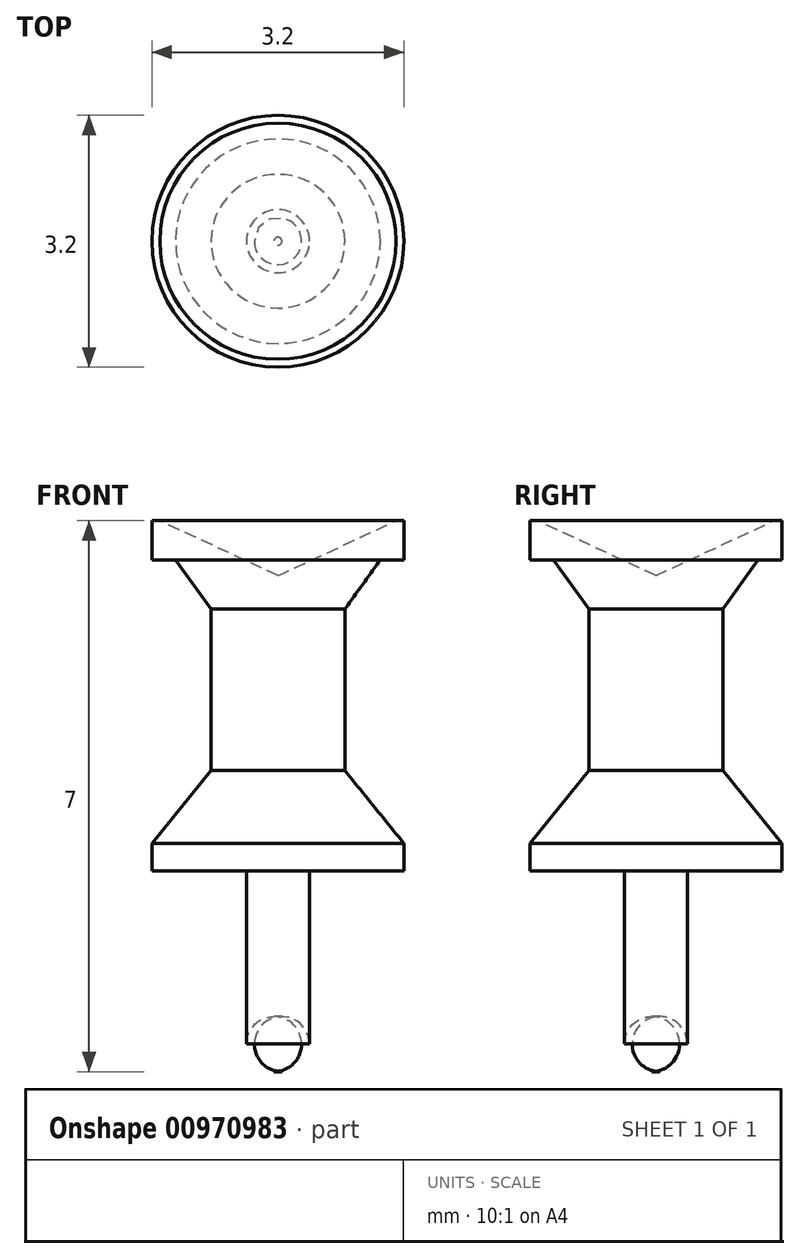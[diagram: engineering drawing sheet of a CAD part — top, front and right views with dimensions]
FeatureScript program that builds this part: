
annotation { "Feature Type Name" : "Feature", "Feature Type Description" : "" }
export const myFeature = defineFeature(function(context is Context, id is Id, definition is map)
    precondition{}
    {
        {
            var Q0;
            Q0=qCreatedBy(makeId("Front.planeOp"),FACE);
            var sketch = newSketch(context, id + "F0", { "sketchPlane" : qUnion([Q0])});
            skLineSegment(sketch, "E0", {"start": v(1.6, 4.45) * mm, "end": v(1.6, 3.95) * mm});
            skLineSegment(sketch, "E1", {"start": v(1.6, 4.45) * mm, "end": v(1.5, 4.45) * mm});
            skLineSegment(sketch, "E2", {"start": v(1.5, 4.45) * mm, "end": v(0, 3.75) * mm});
            skLineSegment(sketch, "E3", {"start": v(1.6, 4.45) * mm, "end": v(1.6, 3.95) * mm, "construction": true});
            skLineSegment(sketch, "E4", {"start": v(1.6, 3.95) * mm, "end": v(1.3, 3.95) * mm});
            skLineSegment(sketch, "E5", {"start": v(1.3, 3.95) * mm, "end": v(0.85, 3.33) * mm});
            skLineSegment(sketch, "E6", {"start": v(1.6, 0.35) * mm, "end": v(0.85, 1.27) * mm});
            skLineSegment(sketch, "E7", {"start": v(0.85, 4.45) * mm, "end": v(0.85, 1.27) * mm, "construction": true});
            skLineSegment(sketch, "E8", {"start": v(0.85, 3.33) * mm, "end": v(0.85, 1.27) * mm});
            skLineSegment(sketch, "E9.trimOffspring", {"start": v(1.6, 0.35) * mm, "end": v(1.6, 0) * mm, "construction": true});
            skLineSegment(sketch, "E10", {"start": v(1.6, 0.35) * mm, "end": v(1.6, 0) * mm});
            skLineSegment(sketch, "E11", {"start": v(0.4, 0) * mm, "end": v(1.6, 0) * mm});
            skPoint(sketch, "E12.start.orphan", {"position": v(0, 0) * mm});
            skLineSegment(sketch, "E13", {"start": v(0.4, 0) * mm, "end": v(0.4, -2.05) * mm});
            skLineSegment(sketch, "E14", {"start": v(0, -2.4) * mm, "end": v(0, 3.75) * mm});
            skLineSegment(sketch, "E15", {"start": v(1.6, 4.45) * mm, "end": v(0, 4.45) * mm, "construction": true});
            skLineSegment(sketch, "E16", {"start": v(0, 4.45) * mm, "end": v(0, -2.55) * mm, "construction": true});
            skLineSegment(sketch, "E17", {"start": v(0.4, -2.05) * mm, "end": v(0.4, -2.2) * mm});
            skLineSegment(sketch, "E18", {"start": v(0.05, -2.55) * mm, "end": v(0, -2.55) * mm});
            skLineSegment(sketch, "E19", {"start": v(0, -2.4) * mm, "end": v(0, -2.55) * mm});
            skPoint(sketch, "E20.visualSharp", {"position": v(0.4, -2.55) * mm});
            skArc(sketch, "E20.filletArc", {"start": v(0.05, -2.55) * mm, "mid": v(0.3, -2.45) * mm, "end": v(0.4, -2.2) * mm});
            skSolve(sketch);
        }
        {
            var Q0;
            Q0=sQuery(id+"F0.wireOp",EDGE,"E18");
            var Q1;
            Q1=sQuery(id+"F0.wireOp",EDGE,"E20.filletArc");
            var Q2;
            Q2=sQuery(id+"F0.wireOp",EDGE,"E17");
            var Q3;
            Q3=sQuery(id+"F0.wireOp",EDGE,"E13");
            var Q4;
            Q4=sQuery(id+"F0.wireOp",EDGE,"E11");
            var Q5;
            Q5=sQuery(id+"F0.wireOp",EDGE,"E10");
            var Q6;
            Q6=sQuery(id+"F0.wireOp",EDGE,"E6");
            var Q7;
            Q7=sQuery(id+"F0.wireOp",EDGE,"E8");
            var Q8;
            Q8=sQuery(id+"F0.wireOp",EDGE,"E5");
            var Q9;
            Q9=sQuery(id+"F0.wireOp",EDGE,"E4");
            var Q10;
            Q10=sQuery(id+"F0.wireOp",EDGE,"E0");
            var Q11;
            Q11=sQuery(id+"F0.wireOp",EDGE,"E1");
            var Q12;
            Q12=sQuery(id+"F0.wireOp",EDGE,"E2");
            var Q13;
            Q13=sQuery(id+"F0.wireOp",EDGE,"E14");
            revolve(context, id + "F1", {"bodyType" : ToolBodyType.SURFACE, "surfaceOperationType" : NewSurfaceOperationType.NEW, "surfaceEntities" : qUnion([Q0, Q1, Q2, Q3, Q4, Q5, Q6, Q7, Q8, Q9, Q10, Q11, Q12]), "axis" : qUnion([Q13]), "revolveType" : RevolveType.FULL});
        }
    });
